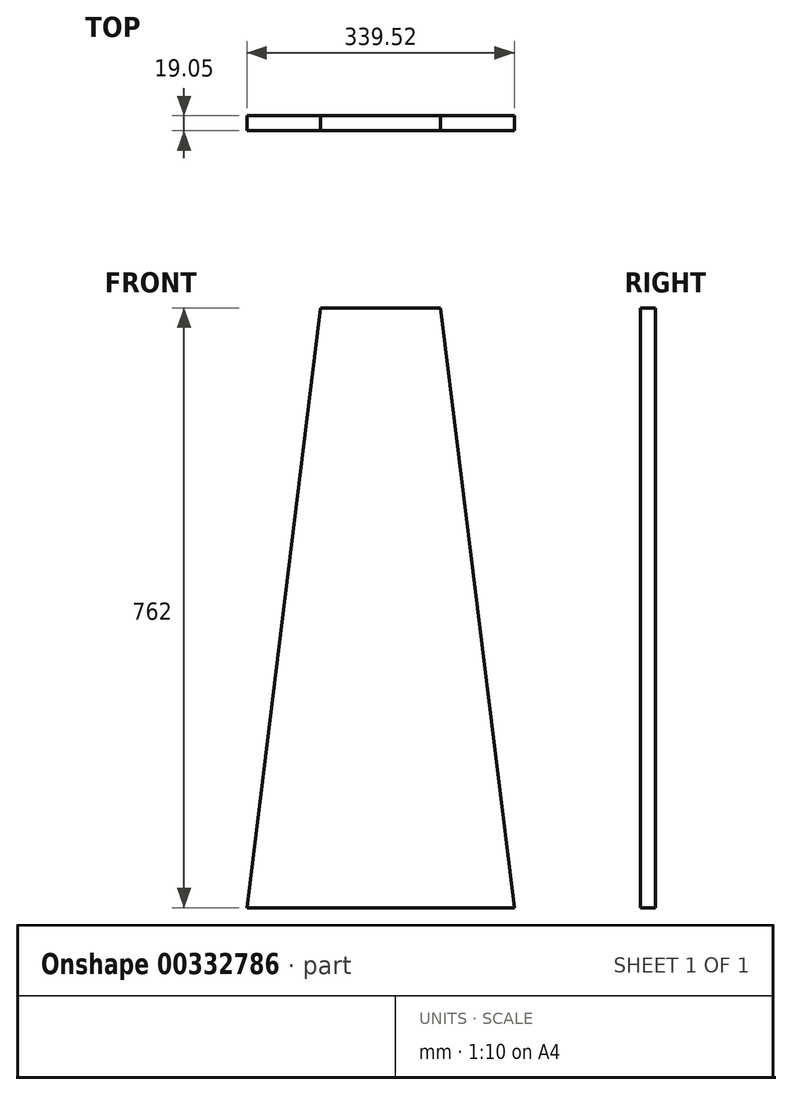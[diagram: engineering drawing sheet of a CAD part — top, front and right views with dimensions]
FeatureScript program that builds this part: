
annotation { "Feature Type Name" : "Feature", "Feature Type Description" : "" }
export const myFeature = defineFeature(function(context is Context, id is Id, definition is map)
    precondition{}
    {
        {
            var Q0;
            Q0=qCreatedBy(makeId("Front.planeOp"),FACE);
            var sketch = newSketch(context, id + "F0", { "sketchPlane" : qUnion([Q0])});
            skLineSegment(sketch, "E0", {"start": v(0, 0) * mm, "end": v(93.56, 762) * mm});
            skLineSegment(sketch, "E1", {"start": v(93.56, 762) * mm, "end": v(245.96, 762) * mm});
            skLineSegment(sketch, "E2", {"start": v(245.96, 762) * mm, "end": v(339.52, 0) * mm});
            skLineSegment(sketch, "E3", {"start": v(339.52, 0) * mm, "end": v(0, 0) * mm});
            skSolve(sketch);
        }
        {
            var Q0;
            Q0=makeQuery(id+"F0.imprint","IMPRINT",FACE,{"disambiguationData":[TD([[makeQuery(id+"F0.imprint","IMPRINT",EDGE,{"derivedFrom":sQuery(id+"F0.wireOp",EDGE,"E0")}),-1.0]])]});
            var Q1;
            Q1 = qSketchRegion(id + "F0", true);
            extrude(context, id + "F1", {"entities" : qUnion([Q0, Q1]), "depth" : 19.05 * mm});
        }
    });
